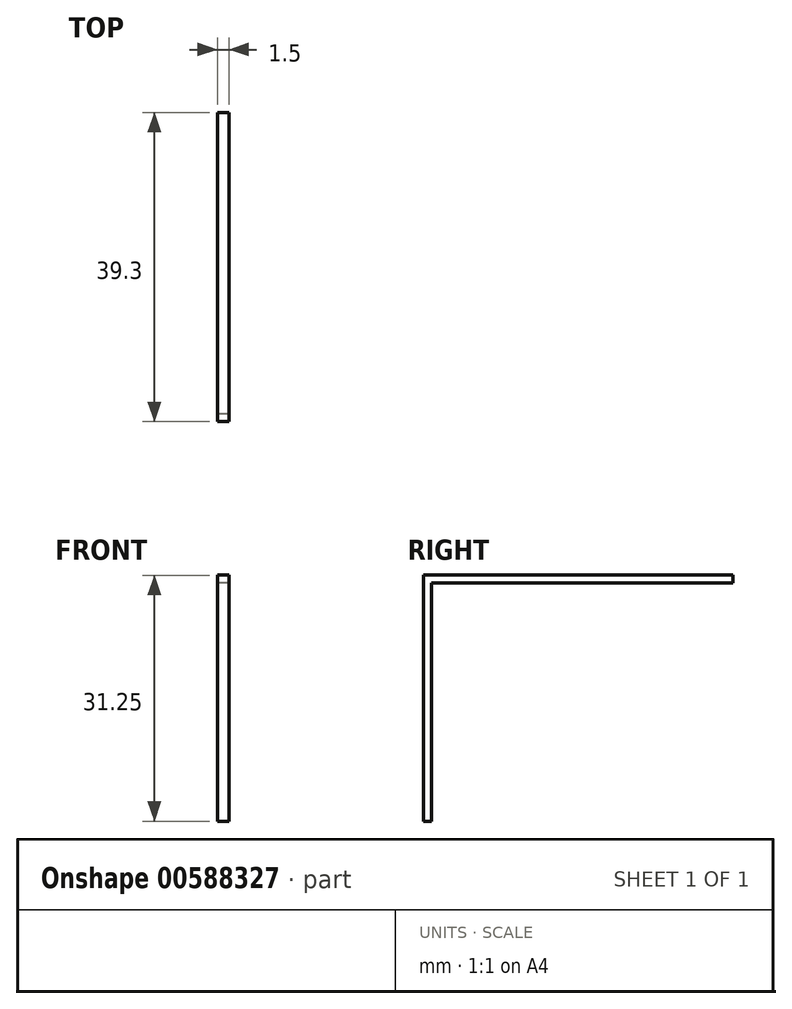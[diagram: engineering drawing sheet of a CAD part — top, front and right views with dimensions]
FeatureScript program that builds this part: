
annotation { "Feature Type Name" : "Feature", "Feature Type Description" : "" }
export const myFeature = defineFeature(function(context is Context, id is Id, definition is map)
    precondition{}
    {
        {
            var Q0;
            Q0=qCreatedBy(makeId("Right.planeOp"),FACE);
            var sketch = newSketch(context, id + "F0", { "sketchPlane" : qUnion([Q0])});
            skLineSegment(sketch, "E0.bottom", {"start": v(-76.15, 14) * mm, "end": v(-115.45, 14) * mm});
            skLineSegment(sketch, "E0.left", {"start": v(-76.15, 14) * mm, "end": v(-76.15, 46.74) * mm});
            skLineSegment(sketch, "E0.right", {"start": v(-115.45, 14) * mm, "end": v(-115.45, 46.74) * mm});
            skLineSegment(sketch, "E1", {"start": v(-115.45, 45.24) * mm, "end": v(-76.15, 45.24) * mm});
            skLineSegment(sketch, "E2", {"start": v(-115.45, 45.24) * mm, "end": v(-114.45, 45.24) * mm});
            skLineSegment(sketch, "E3", {"start": v(-114.45, 45.24) * mm, "end": v(-114.45, 14) * mm});
            skLineSegment(sketch, "E4", {"start": v(-114.45, 45.24) * mm, "end": v(-114.45, 44.24) * mm});
            skLineSegment(sketch, "E5", {"start": v(-114.45, 44.24) * mm, "end": v(-76.15, 44.24) * mm});
            skLineSegment(sketch, "E6", {"start": v(-76.15, 44.24) * mm, "end": v(-77.15, 44.24) * mm});
            skLineSegment(sketch, "E7", {"start": v(-77.15, 44.24) * mm, "end": v(-77.15, 14) * mm});
            skSolve(sketch);
        }
        {
            var Q0;
            {var subQ0=sQuery(id+"F0.wireOp",EDGE,"E1");Q0=makeQuery(id+"F0.imprint","IMPRINT",FACE,{"disambiguationData":[TD([[makeQuery(id+"F0.imprint","IMPRINT",EDGE,{"derivedFrom":subQ0}),-1.0]])]});}
            var Q1;
            {var subQ4=sQuery(id+"F0.wireOp",EDGE,"E2");Q1=makeQuery(id+"F0.imprint","IMPRINT",FACE,{"disambiguationData":[TD([[makeQuery(id+"F0.imprint","IMPRINT",EDGE,{"derivedFrom":subQ4}),-1.0]])]});}
            var Q2;
            {var subQ4=sQuery(id+"F0.wireOp",EDGE,"E6");Q2=makeQuery(id+"F0.imprint","IMPRINT",FACE,{"disambiguationData":[TD([[makeQuery(id+"F0.imprint","IMPRINT",EDGE,{"derivedFrom":subQ4}),1.0]])]});}
            extrude(context, id + "F1", {"entities" : qUnion([Q0, Q1, Q2]), "depth" : 1.5 * mm, "offsetDistance" : 25 * mm});
        }
    });
